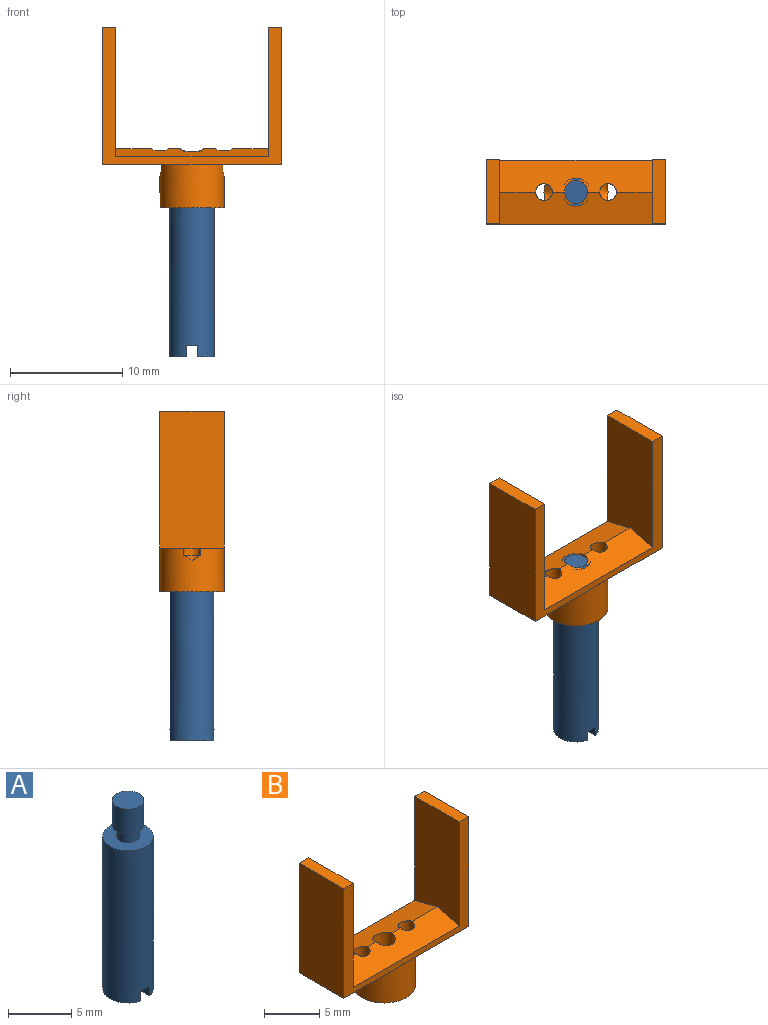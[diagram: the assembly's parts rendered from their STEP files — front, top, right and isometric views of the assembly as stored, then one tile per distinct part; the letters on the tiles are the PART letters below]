
ASSEMBLY  parts=2 mates=1
PART A: 11 faces, bbox 4x4x18.3 mm
  f0: plane 3.87x1.5mm, normal (0,0,-1), area 4.3mm2, adj f7,f8
  f1: plane 3.87x1.5mm, normal (0,0,-1), area 4.3mm2, adj f7,f10
  f2: plane 2.5x2.5mm, normal (0,0,1), area 4.9mm2, adj f3
  f3: cylinder r=1.25mm len=2.5mm, axis (0,0,1), area 18.8mm2, adj f2,f4
  f4: plane 2.5x2.5mm, normal (0,0,-1), area 2.4mm2, adj f3,f5
  f5: cylinder r=0.9mm len=1.8mm, axis (0,0,1), area 6.2mm2, adj f4,f6
  f6: plane 4x4mm, normal (0,0,1), area 10mm2, adj f5,f7
  f7: cylinder r=2mm len=14.75mm, axis (0,0,1), area 183.3mm2, adj f0,f1,f6,f8,f9,f10
  f8: plane 3.87x1mm, normal (-1,0,0), area 3.9mm2, adj f0,f7,f9
  f9: plane 4x1mm, normal (0,0,-1), area 4mm2, adj f7,f8,f10
  f10: plane 3.87x1mm, normal (1,0,0), area 3.9mm2, adj f1,f7,f9
PART B: 21 faces, bbox 16x5.7x16.1 mm
  f0: cylinder r=1.03mm len=3.76mm, axis (0,0,1), area 23.2mm2, adj f17,f18,f19
  f1: cylinder r=0.75mm len=2mm, axis (0,0,1), area 7.2mm2, adj f3,f4,f15,f17,f18
  f2: cylinder r=0.75mm len=2mm, axis (0,0,1), area 7.2mm2, adj f3,f5,f16,f17,f18
  f3: cylinder r=2.85mm len=5.7mm, axis (0,0,-1), area 67.4mm2, adj f1,f2,f4,f5,f14,f15,f16
  f4: plane 8x5.7mm, normal (0,0,-1), area 31.9mm2, adj f1,f3,f6,f12,f13
  f5: plane 8x5.7mm, normal (0,0,-1), area 31.9mm2, adj f2,f3,f11,f12,f13
  f6: plane 12.18x5.7mm, normal (1,0,0), area 69.4mm2, adj f4,f7,f12,f13
  f7: plane 5.7x1.2mm, normal (0,0,1), area 6.8mm2, adj f6,f8,f12,f13
  f8: plane 11.53x5.7mm, normal (-1,0,0), area 63.7mm2, adj f7,f12,f13,f17,f18
  f9: plane 11.53x5.7mm, normal (1,0,0), area 63.7mm2, adj f10,f12,f13,f17,f18
  f10: plane 5.7x1.2mm, normal (0,0,1), area 6.8mm2, adj f9,f11,f12,f13
  f11: plane 12.18x5.7mm, normal (-1,0,0), area 69.4mm2, adj f5,f10,f12,f13
  f12: plane 16x12.18mm, normal (0,-1,0), area 38.1mm2, adj f4,f5,f6,f7,f8,f9,f10,f11
  f13: plane 16x12.18mm, normal (0,1,0), area 38.1mm2, adj f4,f5,f6,f7,f8,f9,f10,f11
  f14: plane 5.7x5.7mm, normal (0,0,-1), area 13mm2, adj f3,f20
  f15: cone r=0mm half-angle=59deg, axis (0,0,1), area 1mm2, adj f1,f3
  f16: cone r=0mm half-angle=59deg, axis (0,0,1), area 1mm2, adj f2,f3
  f17: plane 13.6x2.85mm, normal (0,-0.24,0.97), area 36.4mm2, adj f0,f1,f2,f8,f9,f12,f18
  f18: plane 13.6x2.85mm, normal (0,0.24,0.97), area 36.4mm2, adj f0,f1,f2,f8,f9,f13,f17
  f19: plane 4x4mm, normal (0,0,-1), area 9.3mm2, adj f0,f20
  f20: cylinder r=2mm len=4mm, axis (0,0,-1), area 18.8mm2, adj f14,f19
PLACE A t=(0,0,-18.25)mm
PLACE B t=(0,0,-5)mm
MATE fastened A.f3 <-> B.f0  axis (0,0,1) through (0,0,-3.5)mm
